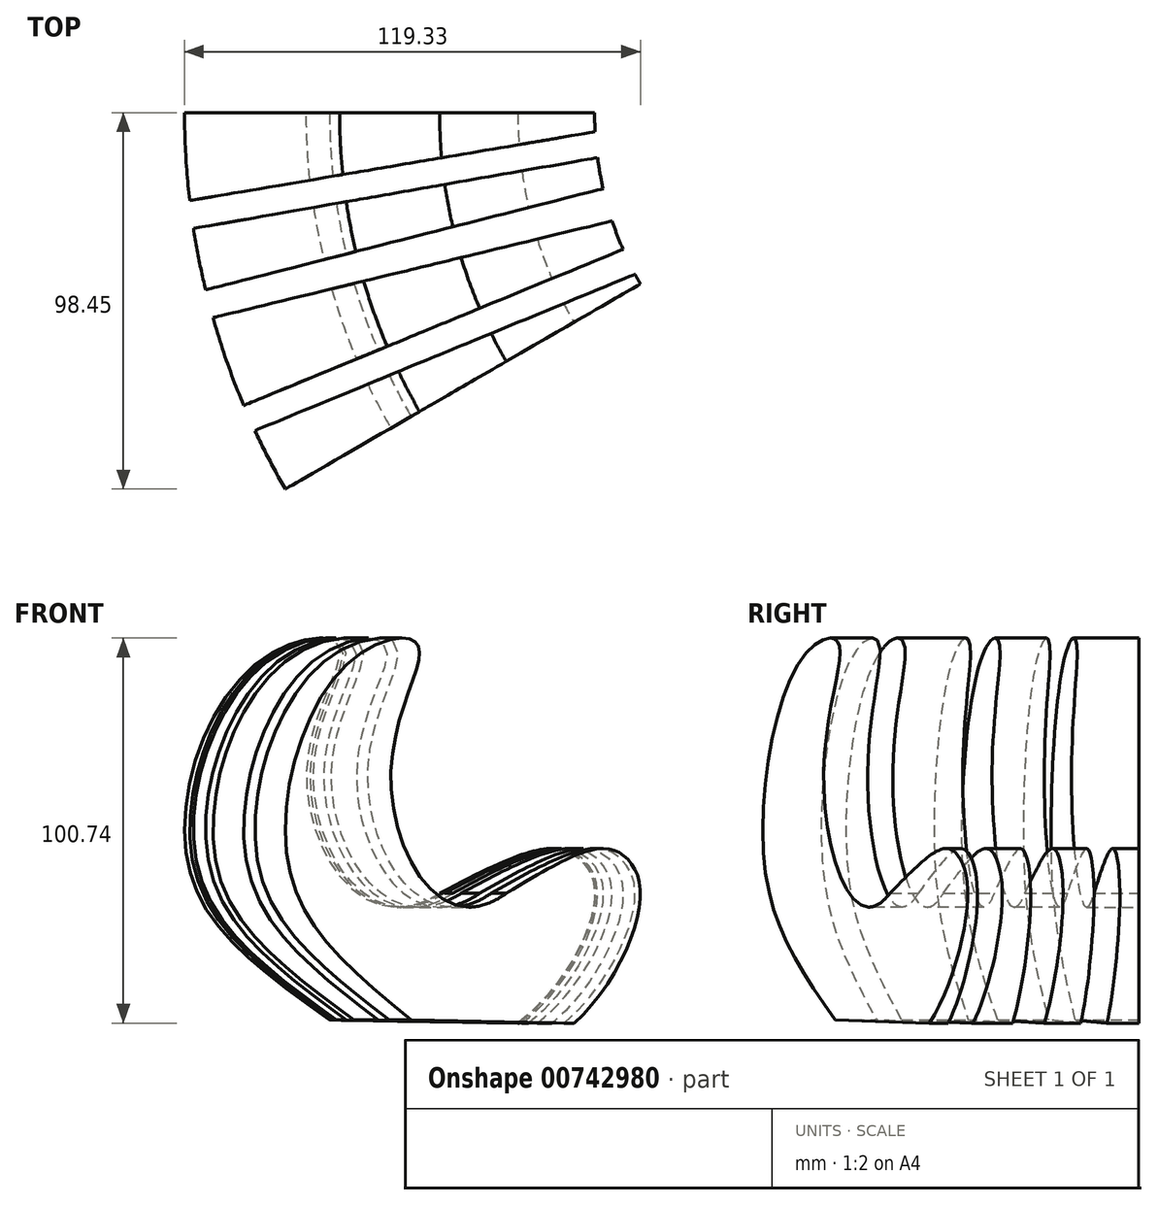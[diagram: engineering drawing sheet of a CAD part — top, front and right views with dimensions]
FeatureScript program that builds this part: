
annotation { "Feature Type Name" : "Feature", "Feature Type Description" : "" }
export const myFeature = defineFeature(function(context is Context, id is Id, definition is map)
    precondition{}
    {
        {
            var Q0;
            Q0=qCreatedBy(makeId("Front.planeOp"),FACE);
            var sketch = newSketch(context, id + "F0", { "sketchPlane" : qUnion([Q0])});
            skFitSpline(sketch, "E0", {"points": [v(-33.11, -76.25) * mm, v(-70.33, -34.74) * mm, v(-52.5, 16.84) * mm, v(-30.97, 21.84) * mm, v(-39.2, -12.89) * mm, v(-4.33, -43.08) * mm], "startDerivative": vector(-249.84, 180.17) * mm, "endDerivative": vector(288.25, 182.51) * mm});
            skFitSpline(sketch, "E1", {"points": [v(-4.33, -43.08) * mm, v(30.56, -32.84) * mm, v(36.24, -43.08) * mm, v(16.15, -77.05) * mm], "startDerivative": vector(176.23, 94.4) * mm, "endDerivative": vector(-89.52, -69.1) * mm});
            skLineSegment(sketch, "E2", {"start": v(-33.11, -76.25) * mm, "end": v(16.15, -77.05) * mm});
            skLineSegment(sketch, "E3", {"start": v(125.81, -86.83) * mm, "end": v(125.81, 291.37) * mm, "construction": true});
            skSolve(sketch);
        }
        {
            var Q0;
            Q0 = qSketchRegion(id + "F0", true);
            var Q1;
            Q1=sQuery(id+"F0.wireOp",EDGE,"E3");
            revolve(context, id + "F1", {"surfaceOperationType" : NewSurfaceOperationType.NEW, "entities" : qUnion([Q0]), "axis" : qUnion([Q1]), "revolveType" : RevolveType.ONE_DIRECTION, "angle" : 30 * degree});
        }
        {
            var Q0;
            Q0=qCreatedBy(makeId("Top.planeOp"),FACE);
            var sketch = newSketch(context, id + "F2", { "sketchPlane" : qUnion([Q0])});
            skLineSegment(sketch, "E4", {"start": v(44.47, -3.58) * mm, "end": v(-92.4, -26.81) * mm});
            skLineSegment(sketch, "E5", {"start": v(-92.4, -26.81) * mm, "end": v(-92.4, -34.42) * mm});
            skLineSegment(sketch, "E6", {"start": v(-92.4, -34.42) * mm, "end": v(44.9, -10.34) * mm});
            skLineSegment(sketch, "E7", {"start": v(44.9, -10.34) * mm, "end": v(46.21, -17.86) * mm});
            skLineSegment(sketch, "E8", {"start": v(46.21, -17.86) * mm, "end": v(-88.6, -52.16) * mm});
            skLineSegment(sketch, "E9", {"start": v(-88.6, -52.16) * mm, "end": v(-86.8, -59.2) * mm});
            skLineSegment(sketch, "E10", {"start": v(-86.8, -59.2) * mm, "end": v(47, -26.81) * mm});
            skLineSegment(sketch, "E11", {"start": v(47, -26.81) * mm, "end": v(48.67, -33.68) * mm});
            skLineSegment(sketch, "E12", {"start": v(48.67, -33.68) * mm, "end": v(-78.46, -85.95) * mm});
            skLineSegment(sketch, "E13", {"start": v(-78.46, -85.95) * mm, "end": v(-75.71, -92.63) * mm});
            skLineSegment(sketch, "E14", {"start": v(-75.71, -92.63) * mm, "end": v(62.53, -35.78) * mm});
            skLineSegment(sketch, "E15", {"start": v(62.53, -35.78) * mm, "end": v(62.53, -10.34) * mm});
            skLineSegment(sketch, "E16", {"start": v(62.53, -10.34) * mm, "end": v(44.47, -3.58) * mm});
            skSolve(sketch);
        }
        {
            var Q0;
            Q0 = qSketchRegion(id + "F2", true);
            extrude(context, id + "F3", {"entities" : qUnion([Q0]), "endBound" : BoundingType.SYMMETRIC, "depth" : 302.26 * mm, "offsetDistance" : 25.4 * mm});
        }
        {
            var Q0;
            Q0=makeQuery(id+"F3.opExtrude","SWEPT_BODY",BODY,{"disambiguationData":[OSD([sQuery(id+"F2.wireOp",EDGE,"E4"),sQuery(id+"F2.wireOp",EDGE,"E5"),sQuery(id+"F2.wireOp",EDGE,"E6"),sQuery(id+"F2.wireOp",EDGE,"E7"),sQuery(id+"F2.wireOp",EDGE,"E8"),sQuery(id+"F2.wireOp",EDGE,"E9"),sQuery(id+"F2.wireOp",EDGE,"E10"),sQuery(id+"F2.wireOp",EDGE,"E11"),sQuery(id+"F2.wireOp",EDGE,"E12"),sQuery(id+"F2.wireOp",EDGE,"E13"),sQuery(id+"F2.wireOp",EDGE,"E14"),sQuery(id+"F2.wireOp",EDGE,"E15"),sQuery(id+"F2.wireOp",EDGE,"E16")])]});
            var Q1;
            Q1=makeQuery(id+"F1.opRevolve","SWEPT_BODY",BODY,{"disambiguationData":[OSD([sQuery(id+"F0.wireOp",EDGE,"E0"),sQuery(id+"F0.wireOp",EDGE,"E1"),sQuery(id+"F0.wireOp",EDGE,"E2")])]});
            booleanBodies(context, id + "F4", {"operationType" : BooleanOperationType.SUBTRACTION, "tools" : qUnion([Q0]), "targets" : qUnion([Q1])});
        }
    });
